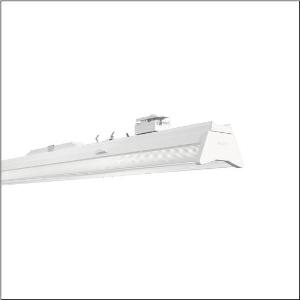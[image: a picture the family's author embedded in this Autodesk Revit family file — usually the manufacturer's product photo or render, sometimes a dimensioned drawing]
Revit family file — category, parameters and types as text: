
# Revit family: licross_r__21_performance_mo_52tm16cn445g_ee6e
name_source: partatom
category: Lighting Fixtures
units: mm (PartAtom-declared; Revit-internal decimal feet)

## family parameters
Cut with Voids When Loaded = No
Host = Face
Light Source = No
Part Type = Normal
Room Calculation Point = No
Round Connector Dimension = Use Diameter
Shared = No

## types (1)
- --- (1 x LED, 4500 lm, 24.1 W, 4000K)
    Apparent Load = 24 VA
    CIE Flux Codes = 66 88 96 79 100
    Color Rendering = 80
    Color Temperature = 4000K
    Default Elevation = 1800 mm
    Description = Licross® 21 Performance MO, luminaire insert, of sheet steel, galvanised, coil coated, white, length: 1.500mm, width: 120mm, height: 123mm, LED rated luminous flux: 4.500lm, light colour: 840, control gear: ON/OFF Multilumen, CLOi, control gear: ECG Multilumen, with plug, 3-pole, with phase selection, mains connection: 220..240V, AC, 50/60Hz, start of lifetime: 24W, end of service life: 28W, halogen-free wiring, primary light control with lens, of plastic, primary optical cover: cover, of PMMA, CAT 2 (L<= 3000cd/m²), light emission: direct/indirect distribution, primary light characteristic: symmetric, protection rating (complete): IP40, insulation class (complete): insulation class I (protective earthing), certification: CE, ENEC, UKCA, protection symbol: D if used in an environment without relevant dust loads with corresponding accessories, impact resistance: IK06, permissible ambient temperature for indoor applications: -35..+55°C, corresponds to IFS (International Featured Standards) requirements for safety and quality in the food industry, reducing of maximum allowable ambient temperature of 5°C with ceiling mounting, LABS conformity tested according to VDMA 24364:2018-05, packaging unit: 1 piece
    Height = 114 mm
    Lamp = 1 x LED
    Lamp Light Flux = 4500 lm
    Lamp Power = 24.1 W
    Lamp count = 1
    Length = 1500 mm
    Luminous efficacy = 187 lm/W
    Manufacturer = Siteco
    ModVariant = No
    Model = 52TM16CN445G
    Mounting Place = Ceiling
    Mounting Type = Pendant
    Number of Poles = 1
    OnlyDefault = Yes
    Power Factor = 1
    Product Name = Licross® 21 Performance MO
    Product group = luminaire insert
    ProductGroupID = 901
    Protection Class = Protection class I
    Protection Degree = IP 40
    RLX_Detail_Level = 1
    RLX_Emergency_Light_Flux = 0 lm
    RLX_Emergency_Type = 0
    RLX_Emergency_Type_DB = No
    RlxData = <blob elided: 31453 chars, md5=37b1a8a4>
    Socket = socket
    Standby Power = 0 W
    System Light Flux = 4500 lm
    System Power = 24 W
    Type Comments = factory setting: luminous flux: 100 % | (A | C | E) | 55 mA
    Type Image = l_1256138.jpg
    URL = http://relux.com
    VarID = @adj_007015
    Voltage = 0 V
    Weight = 0.00 kg
    Width = 120 mm

## geometry (parser evidence)
native form markers: Blend x4, Sweep x12
no freeform markers — native parametric forms only
